# Revit family: 06-30-030 DN700-1200
name_source: partatom
category: Pipe Accessories
units: mm (PartAtom-declared; Revit-internal decimal feet)

## family parameters
Always vertical = No
Cut with Voids When Loaded = No
Part Type = Valve - Breaks Into
Round Connector Dimension = Use Diameter
Shared = No
Work Plane-Based = No

## types (10) — shared parameters
10 = 10 mm  [stored 0.0328084 ft]
2 = 2 mm  [stored 0.00656168 ft]
20 = 20 mm  [stored 0.0656168 ft]
Actuator_FL_T = 20 mm  [stored 0.0656168 ft]
Body_Radius1 = 85 mm
Bonnet_W = 167.5 mm
Bypass_ H = 282 mm
Bypass_Body_BotmH = 11.75 mm  [stored 0.0385499 ft]
Bypass_Body_H = 108 mm
Bypass_Bonnet_L = 173 mm
Bypass_Connection_end = 51.7 mm  [stored 0.169619 ft]
Bypass_pipe_R = 47 mm  [stored 0.154199 ft]
DN1000_ PN10 = 06-1000-30-090431641
DN1000_ PN16 = 06-1000-30-091431641
DN1200_ PN10 = 06-1200-30-090431181
DN1200_ PN16 = 06-1200-30-091431181
DN700_ PN10 = 06-700-30-0046411
DN700_ PN16 = 06-700-30-0146411
DN800_ PN10 = 06-800-30-0046411
DN800_ PN16 = 06-800-30-0146411
DN900_ PN10 = 06-900-30-0046411
DN900_ PN16 = 06-900-30-0146411
Description_ = AVK FLANGED GATE VALVE, PN10/16
F1 = 103 mm
F3 = 148 mm
Gland_FL_R = 130.65 mm
Raised_dis = 5 mm  [stored 0.0164042 ft]
Search_table = 06-30-030 DN700-1200
URL product pages = https://www.avkvalves.com
zero-valued in all types: Default Elevation

## per-type parameters (varying)
- DN0700_ PN10: Actuator_FLR=105 mm; Actuator_FL_Support=63 mm; Actuator_H=121.5 mm; Actuator_dim1=81.9 mm; Body_Bottom_H=106.05 mm; Body_FL_L=596 mm; Body_FL_T=72 mm; Body_FL_W=252.5 mm; Body_Height=780 mm; Body_L=546.5 mm; Body_Radius=60 mm  [stored 0.19685 ft]; Body_Rib=246.4 mm; Body_T=23 mm  [stored 0.0754593 ft]; Body_W=176.75 mm; Bonet_L=491.85 mm; Bonnet_FL_W=252.5 mm; Bonnet_H=491.85 mm; Bore=350 mm; Bypass_Body_L=63.75 mm; Bypass_Body_W=31.88 mm; Bypass_Bonnet_FL_L=75 mm; Bypass_Bonnet_W=39.84 mm; Bypass_StoS=695 mm; D2=20 mm  [stored 0.0656168 ft]; D22=7.81 mm; DN=700 mm; F2=81 mm; F22=48.6 mm  [stored 0.159449 ft]; FL_T=36 mm  [stored 0.11811 ft]; Gland_FL_T=45 mm  [stored 0.147638 ft]; Gland_Flange_Bypass=22.31 mm; H=1622 mm; H3=2070 mm; H3-H=448 mm; L=505 mm; L2=327.9 mm; OD=448 mm; Raised_Radius=403.2 mm; Rib_H=201 mm; Rib_H1=109 mm; Rib_L=576.67 mm; Rib_T=17.5 mm  [stored 0.0574147 ft]; Rib_W=194.43 mm; W=1375 mm; W-W1=605 mm; W1=770 mm; W2=95.63 mm; logo=86.4 mm; sweep_path_W=114.89 mm
- DN0700_ PN16: Actuator_FLR=105 mm; Actuator_FL_Support=63 mm; Actuator_H=121.5 mm; Actuator_dim1=81.9 mm; Body_Bottom_H=106.05 mm; Body_FL_L=596 mm; Body_FL_T=72 mm; Body_FL_W=252.5 mm; Body_Height=780 mm; Body_L=546.5 mm; Body_Radius=60 mm  [stored 0.19685 ft]; Body_Rib=250.25 mm; Body_T=23 mm  [stored 0.0754593 ft]; Body_W=176.75 mm; Bonet_L=491.85 mm; Bonnet_FL_W=252.5 mm; Bonnet_H=491.85 mm; Bore=350 mm; Bypass_Body_L=73.1 mm; Bypass_Body_W=36.55 mm  [stored 0.119915 ft]; Bypass_Bonnet_FL_L=86 mm; Bypass_Bonnet_W=45.69 mm; Bypass_StoS=720 mm; D2=20 mm  [stored 0.0656168 ft]; D22=8.95 mm; DN=700.1 mm; F2=81 mm; F22=48.6 mm  [stored 0.159449 ft]; FL_T=36 mm  [stored 0.11811 ft]; Gland_FL_T=45 mm  [stored 0.147638 ft]; Gland_Flange_Bypass=25.59 mm; H=1622 mm; H3=2077 mm; H3-H=455 mm; L=505 mm; L2=327.9 mm; OD=455 mm; Raised_Radius=409.5 mm; Rib_H=201 mm; Rib_H1=109 mm; Rib_L=576.67 mm; Rib_T=17.5 mm  [stored 0.0574147 ft]; Rib_W=194.43 mm; W=1412 mm; W-W1=606 mm; W1=806 mm; W2=109.65 mm; logo=86.4 mm; sweep_path_W=114.89 mm
- DN0800_ PN10: Actuator_FLR=105 mm; Actuator_FL_Support=63 mm; Actuator_H=121.5 mm; Actuator_dim1=81.9 mm; Body_Bottom_H=114.66 mm; Body_FL_L=596 mm; Body_FL_T=72 mm; Body_FL_W=273 mm; Body_Height=830 mm; Body_L=543.5 mm; Body_Radius=65 mm; Body_Rib=279.4 mm; Body_T=35 mm  [stored 0.114829 ft]; Body_W=191.1 mm; Bonet_L=489.15 mm; Bonnet_FL_W=273 mm; Bonnet_H=489.15 mm; Bore=400 mm; Bypass_Body_L=68 mm; Bypass_Body_W=34 mm; Bypass_Bonnet_FL_L=80 mm; Bypass_Bonnet_W=42.5 mm; Bypass_StoS=802 mm; D2=20 mm  [stored 0.0656168 ft]; D22=8.33 mm; DN=800 mm; F2=81 mm; F22=48.6 mm  [stored 0.159449 ft]; FL_T=41 mm  [stored 0.134514 ft]; Gland_FL_T=53 mm  [stored 0.173885 ft]; Gland_Flange_Bypass=23.8 mm; H=1672 mm; H3=2180 mm; H3-H=508 mm; L=546 mm; L2=326.1 mm; OD=508 mm; Raised_Radius=457.2 mm; Rib_H=170 mm; Rib_H1=110 mm; Rib_L=568.1 mm; Rib_T=15 mm  [stored 0.0492126 ft]; Rib_W=210.21 mm; W=1487 mm; W-W1=605 mm; W1=882 mm; W2=102 mm; logo=86.4 mm; sweep_path_W=124.22 mm
- DN0800_ PN16: Actuator_FLR=105 mm; Actuator_FL_Support=63 mm; Actuator_H=121.5 mm; Actuator_dim1=81.9 mm; Body_Bottom_H=106.05 mm; Body_FL_L=596 mm; Body_FL_T=72 mm; Body_FL_W=252.5 mm; Body_Height=830 mm; Body_L=543.5 mm; Body_Radius=65 mm; Body_Rib=282.15 mm; Body_T=35 mm  [stored 0.114829 ft]; Body_W=176.75 mm; Bonet_L=489.15 mm; Bonnet_FL_W=252.5 mm; Bonnet_H=489.15 mm; Bore=400 mm; Bypass_Body_L=73.1 mm; Bypass_Body_W=36.55 mm  [stored 0.119915 ft]; Bypass_Bonnet_FL_L=86 mm; Bypass_Bonnet_W=45.69 mm; Bypass_StoS=735 mm; D2=20 mm  [stored 0.0656168 ft]; D22=8.95 mm; DN=800.1 mm; F2=81 mm; F22=48.6 mm  [stored 0.159449 ft]; FL_T=41 mm  [stored 0.134514 ft]; Gland_FL_T=53 mm  [stored 0.173885 ft]; Gland_Flange_Bypass=25.59 mm; H=1672 mm; H3=2185 mm; H3-H=513 mm; L=505 mm; L2=326.1 mm; OD=513 mm; Raised_Radius=461.7 mm; Rib_H=170 mm; Rib_H1=110 mm; Rib_L=568.1 mm; Rib_T=15 mm  [stored 0.0492126 ft]; Rib_W=194.43 mm; W=1427 mm; W-W1=606 mm; W1=821 mm; W2=109.65 mm; logo=86.4 mm; sweep_path_W=114.89 mm
- DN0900_ PN10: Actuator_FLR=105 mm; Actuator_FL_Support=63 mm; Actuator_H=121.5 mm; Actuator_dim1=81.9 mm; Body_Bottom_H=134.61 mm; Body_FL_L=757.5 mm; Body_FL_T=94 mm; Body_FL_W=320.5 mm; Body_Height=1088 mm; Body_L=677.5 mm; Body_Radius=75 mm; Body_Rib=306.9 mm; Body_T=40 mm  [stored 0.131234 ft]; Body_W=224.35 mm; Bonet_L=609.75 mm; Bonnet_FL_W=320.5 mm; Bonnet_H=609.75 mm; Bore=450 mm; Bypass_Body_L=73.1 mm; Bypass_Body_W=36.55 mm  [stored 0.119915 ft]; Bypass_Bonnet_FL_L=86 mm; Bypass_Bonnet_W=45.69 mm; Bypass_StoS=880 mm; D2=20 mm  [stored 0.0656168 ft]; D22=8.95 mm; DN=900 mm; F2=81 mm; F22=48.6 mm  [stored 0.159449 ft]; FL_T=35.5 mm  [stored 0.11647 ft]; Gland_FL_T=53 mm  [stored 0.173885 ft]; Gland_Flange_Bypass=25.59 mm; H=2117 mm; H3=2675 mm; H3-H=558 mm; L=641 mm; L2=406.5 mm; OD=558 mm; Raised_Radius=502.2 mm; Rib_H=205 mm; Rib_H1=200 mm; Rib_L=721.43 mm; Rib_T=25 mm  [stored 0.082021 ft]; Rib_W=246.79 mm; W=1728 mm; W-W1=762 mm; W1=966 mm; W2=109.65 mm; logo=112.8 mm; sweep_path_W=145.83 mm
- DN0900_ PN16: Actuator_FLR=105 mm; Actuator_FL_Support=63 mm; Actuator_H=121.5 mm; Actuator_dim1=81.9 mm; Body_Bottom_H=134.61 mm; Body_FL_L=757.5 mm; Body_FL_T=94 mm; Body_FL_W=320.5 mm; Body_Height=1088 mm; Body_L=677.5 mm; Body_Radius=75 mm; Body_Rib=309.65 mm; Body_T=40 mm  [stored 0.131234 ft]; Body_W=224.35 mm; Bonet_L=609.75 mm; Bonnet_FL_W=320.5 mm; Bonnet_H=609.75 mm; Bore=450 mm; Bypass_Body_L=73.1 mm; Bypass_Body_W=36.55 mm  [stored 0.119915 ft]; Bypass_Bonnet_FL_L=86 mm; Bypass_Bonnet_W=45.69 mm; Bypass_StoS=880 mm; D2=20 mm  [stored 0.0656168 ft]; D22=8.95 mm; DN=900.1 mm; F2=81 mm; F22=48.6 mm  [stored 0.159449 ft]; FL_T=35.5 mm  [stored 0.11647 ft]; Gland_FL_T=53 mm  [stored 0.173885 ft]; Gland_Flange_Bypass=25.59 mm; H=2117 mm; H3=2680 mm; H3-H=563 mm; L=641 mm; L2=406.5 mm; OD=563 mm; Raised_Radius=506.7 mm; Rib_H=205 mm; Rib_H1=200 mm; Rib_L=721.43 mm; Rib_T=25 mm  [stored 0.082021 ft]; Rib_W=246.79 mm; W=1728 mm; W-W1=762 mm; W1=966 mm; W2=109.65 mm; logo=112.8 mm; sweep_path_W=145.83 mm
- DN1000_ PN10: Actuator_FLR=105 mm; Actuator_FL_Support=63 mm; Actuator_H=121.5 mm; Actuator_dim1=81.9 mm; Body_Bottom_H=134.61 mm; Body_FL_L=757.5 mm; Body_FL_T=94 mm; Body_FL_W=320.5 mm; Body_Height=1038 mm; Body_L=677.5 mm; Body_Radius=75 mm; Body_Rib=338.25 mm; Body_T=40 mm  [stored 0.131234 ft]; Body_W=224.35 mm; Bonet_L=609.75 mm; Bonnet_FL_W=320.5 mm; Bonnet_H=609.75 mm; Bore=500 mm; Bypass_Body_L=73.1 mm; Bypass_Body_W=36.55 mm  [stored 0.119915 ft]; Bypass_Bonnet_FL_L=86 mm; Bypass_Bonnet_W=45.69 mm; Bypass_StoS=920 mm; D2=20 mm  [stored 0.0656168 ft]; D22=8.95 mm; DN=1000 mm; F2=81 mm; F22=48.6 mm  [stored 0.159449 ft]; FL_T=41 mm  [stored 0.134514 ft]; Gland_FL_T=53 mm  [stored 0.173885 ft]; Gland_Flange_Bypass=25.59 mm; H=2067 mm; H3=2682 mm; H3-H=615 mm; L=641 mm; L2=406.5 mm; OD=615 mm; Raised_Radius=553.5 mm; Rib_H=238 mm; Rib_H1=151 mm; Rib_L=721.43 mm; Rib_T=25 mm  [stored 0.082021 ft]; Rib_W=246.79 mm; W=1768 mm; W-W1=762 mm; W1=1006 mm; W2=109.65 mm; logo=112.8 mm; sweep_path_W=145.83 mm
- DN1000_ PN16: Actuator_FLR=105 mm; Actuator_FL_Support=63 mm; Actuator_H=121.5 mm; Actuator_dim1=81.9 mm; Body_Bottom_H=134.61 mm; Body_FL_L=757.5 mm; Body_FL_T=94 mm; Body_FL_W=320.5 mm; Body_Height=1038 mm; Body_L=677.5 mm; Body_Radius=75 mm; Body_Rib=345.4 mm; Body_T=40 mm  [stored 0.131234 ft]; Body_W=224.35 mm; Bonet_L=609.75 mm; Bonnet_FL_W=320.5 mm; Bonnet_H=609.75 mm; Bore=500 mm; Bypass_Body_L=73.1 mm; Bypass_Body_W=36.55 mm  [stored 0.119915 ft]; Bypass_Bonnet_FL_L=86 mm; Bypass_Bonnet_W=45.69 mm; Bypass_StoS=920 mm; D2=20 mm  [stored 0.0656168 ft]; D22=8.95 mm; DN=1000.1 mm; F2=81 mm; F22=48.6 mm  [stored 0.159449 ft]; FL_T=41 mm  [stored 0.134514 ft]; Gland_FL_T=53 mm  [stored 0.173885 ft]; Gland_Flange_Bypass=25.59 mm; H=2067 mm; H3=2695 mm; H3-H=628 mm; L=641 mm; L2=406.5 mm; OD=628 mm; Raised_Radius=565.2 mm; Rib_H=238 mm; Rib_H1=151 mm; Rib_L=721.43 mm; Rib_T=25 mm  [stored 0.082021 ft]; Rib_W=246.79 mm; W=1768 mm; W-W1=762 mm; W1=1006 mm; W2=109.65 mm; logo=112.8 mm; sweep_path_W=145.83 mm
- DN1200_ PN10: Actuator_FLR=150 mm; Actuator_FL_Support=90 mm; Actuator_H=165 mm; Actuator_dim1=117 mm; Body_Bottom_H=132.3 mm; Body_FL_L=935 mm; Body_FL_T=94 mm; Body_FL_W=375 mm; Body_Height=1262 mm; Body_L=809.5 mm; Body_Radius=80 mm; Body_Rib=409.75 mm; Body_T=40 mm  [stored 0.131234 ft]; Body_W=220.5 mm; Bonet_L=728.55 mm; Bonnet_FL_W=375 mm; Bonnet_H=728.55 mm; Bore=600 mm; Bypass_Body_L=73.1 mm; Bypass_Body_W=36.55 mm  [stored 0.119915 ft]; Bypass_Bonnet_FL_L=86 mm; Bypass_Bonnet_W=45.69 mm; Bypass_StoS=1050 mm; D2=25 mm  [stored 0.082021 ft]; D22=8.95 mm; DN=1200 mm; F2=110 mm; F22=66 mm; FL_T=41 mm  [stored 0.134514 ft]; Gland_FL_T=53 mm  [stored 0.173885 ft]; Gland_Flange_Bypass=25.59 mm; H=2476 mm; H3=3221 mm; H3-H=745 mm; L=630 mm; L2=485.7 mm; OD=745 mm; Raised_Radius=670.5 mm; Rib_H=245 mm; Rib_H1=196 mm; Rib_L=890.48 mm; Rib_T=27.5 mm  [stored 0.0902231 ft]; Rib_W=242.55 mm; W=2072 mm; W-W1=936 mm; W1=1136 mm; W2=109.65 mm; logo=112.8 mm; sweep_path_W=143.33 mm
- DN1200_ PN16: Actuator_FLR=150 mm; Actuator_FL_Support=90 mm; Actuator_H=165 mm; Actuator_dim1=117 mm; Body_Bottom_H=132.3 mm; Body_FL_L=935 mm; Body_FL_T=85 mm; Body_FL_W=375 mm; Body_Height=1262 mm; Body_L=831 mm; Body_Radius=80 mm; Body_Rib=418 mm; Body_T=49 mm  [stored 0.160761 ft]; Body_W=220.5 mm; Bonet_L=747.9 mm; Bonnet_FL_W=375 mm; Bonnet_H=747.9 mm; Bore=600 mm; Bypass_Body_L=90.95 mm; Bypass_Body_W=45.48 mm; Bypass_Bonnet_FL_L=107 mm; Bypass_Bonnet_W=56.84 mm; Bypass_StoS=1050 mm; D2=25 mm  [stored 0.082021 ft]; D22=11.14 mm; DN=1200.1 mm; F2=110 mm; F22=66 mm; FL_T=37.5 mm  [stored 0.123031 ft]; Gland_FL_T=53 mm  [stored 0.173885 ft]; Gland_Flange_Bypass=31.83 mm; H=2476 mm; H3=3236 mm; H3-H=760 mm; L=630 mm; L2=498.6 mm; OD=760 mm; Raised_Radius=684 mm; Rib_H=245 mm; Rib_H1=196 mm; Rib_L=890.48 mm; Rib_T=27.5 mm  [stored 0.0902231 ft]; Rib_W=242.55 mm; W=2092 mm; W-W1=935 mm; W1=1157 mm; W2=136.43 mm; logo=102 mm; sweep_path_W=143.33 mm

note: [stored X ft] marks values corroborated as IEEE doubles in the binary element streams (Revit-internal decimal feet)

## geometry (parser evidence)
native form markers: Sweep x5
no freeform markers — native parametric forms only
